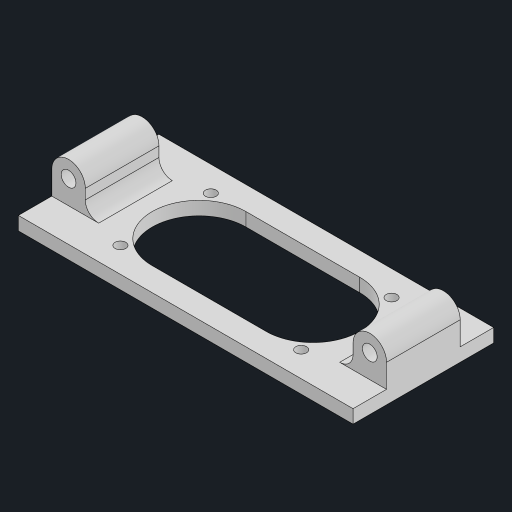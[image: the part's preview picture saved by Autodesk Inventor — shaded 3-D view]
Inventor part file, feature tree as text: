
AUTODESK INVENTOR PART (.ipt)
format: ipt  version: 2023 (Build 270158000, 158)  size: 159,232 bytes
history: native  units: mm
features: extrude x2, other x1, hole x1, fillet x1, mirror x1, sketch x1, projected_geometry x1
ambient origin geometry x8: Origin, YZ Plane, XZ Plane, XY Plane, X Axis, Y Axis, Z Axis, Center Point
bodies: Body1 (feature_tree)
feature tree (8):
  other  "ソリッド1"
  extrude  "押し出し1"  Depth=13.5mm
  hole  "穴1"  [1 undecoded]
  extrude  "押し出し3"  Depth=8.5mm
  fillet  "フィレット2"  Radius=14.0mm
  mirror  "ミラー2"
  sketch  "スケッチ3"
  projected_geometry  "投影ループ1"
note: 1 required parameter value undecoded (feature->parameter linkage not recoverable at this tier; creation-order binding heuristic only, values carry confidence <= 0.55)
